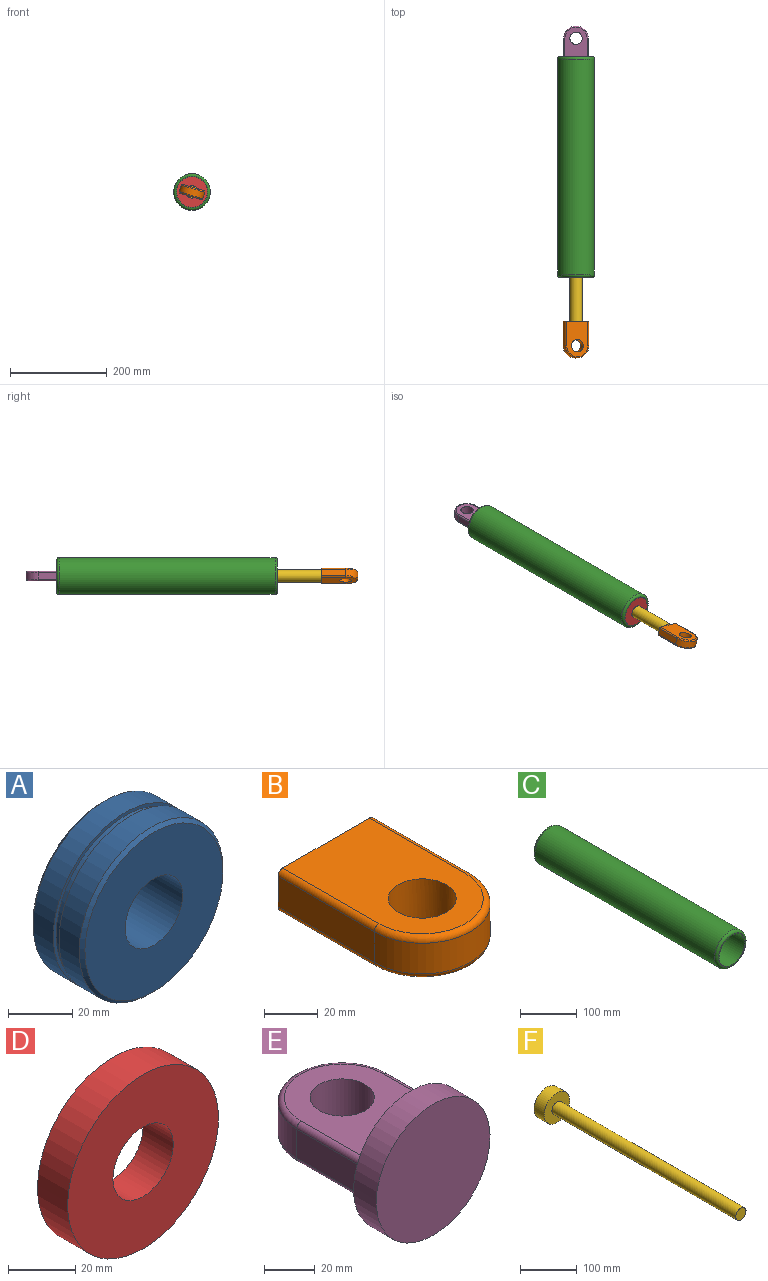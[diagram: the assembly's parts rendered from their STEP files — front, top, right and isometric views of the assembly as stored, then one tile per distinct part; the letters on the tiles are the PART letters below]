
ASSEMBLY  parts=6 mates=5
PART A: 10 faces, bbox 63.5x22.9x63.5 mm
  f0: cylinder r=31.75mm len=63.5mm, axis (0,1,0), area 1773.5mm2, adj f1,f8
  f1: plane 63.5x63.5mm, normal (0,-1,0), area 248.3mm2, adj f0,f3
  f2: plane 60.96x60.96mm, normal (0,1,0), area 2411.9mm2, adj f7,f8
  f3: cylinder r=30.48mm len=60.96mm, axis (0,1,0), area 486.4mm2, adj f1,f6
  f4: cylinder r=31.75mm len=63.5mm, axis (0,1,0), area 1773.5mm2, adj f6,f9
  f5: plane 60.96x60.96mm, normal (0,-1,0), area 2411.9mm2, adj f7,f9
  f6: plane 63.5x63.5mm, normal (0,1,0), area 248.3mm2, adj f3,f4
  f7: cylinder r=12.7mm len=25.4mm, axis (0,-1,0), area 1824.1mm2, adj f2,f5
  f8: cone r=31.75mm half-angle=45deg, axis (0,-1,0), area 351.1mm2, adj f0,f2
  f9: cone r=30.48mm half-angle=45deg, axis (0,1,0), area 351.1mm2, adj f4,f5
PART B: 13 faces, bbox 55x78.3x19.1 mm
  f0: plane 73.66x45.72mm, normal (0,0,1), area 2636.7mm2, adj f4,f6,f7,f8,f9
  f1: plane 50.8x13.97mm, normal (-1,0,0), area 709.7mm2, adj f4,f5,f7,f11
  f2: plane 73.66x45.72mm, normal (0,0,-1), area 2636.7mm2, adj f4,f6,f10,f11,f12
  f3: plane 50.8x13.97mm, normal (1,0,0), area 709.7mm2, adj f4,f5,f8,f10
  f4: plane 50.8x19.05mm, normal (0,1,0), area 962.2mm2, adj f0,f1,f2,f3,f7,f8,f10,f11
  f5: cylinder r=25.4mm len=50.8mm, axis (0,0,-1), area 1114.8mm2, adj f1,f3,f9,f12
  f6: cylinder r=12.7mm len=25.4mm, axis (0,0,-1), area 1520.1mm2, adj f0,f2
  f7: cylinder r=2.54mm len=50.8mm, axis (0,-1,0), area 202.7mm2, adj f0,f1,f4,f9
  f8: cylinder r=2.54mm len=50.8mm, axis (0,1,0), area 202.7mm2, adj f0,f3,f4,f9
  f9: torus R=22.86mm, axis (0,0,1), area 306.8mm2, adj f0,f5,f7,f8
  f10: cylinder r=2.54mm len=50.8mm, axis (0,-1,0), area 202.7mm2, adj f2,f3,f4,f12
  f11: cylinder r=2.54mm len=50.8mm, axis (0,1,0), area 202.7mm2, adj f1,f2,f4,f12
  f12: torus R=22.86mm, axis (0,0,1), area 306.8mm2, adj f2,f5,f10,f11
PART C: 6 faces, bbox 82.5x457.2x82.5 mm
  f0: cylinder r=31.75mm len=457.2mm, axis (0,1,0), area 91207.3mm2, adj f2,f3
  f1: cylinder r=38.1mm len=447.04mm, axis (0,1,0), area 107016.6mm2, adj f4,f5
  f2: plane 66.04x66.04mm, normal (0,-1,0), area 258.4mm2, adj f0,f5
  f3: plane 66.04x66.04mm, normal (0,1,0), area 258.4mm2, adj f0,f4
  f4: torus R=33.02mm, axis (0,-1,0), area 1817.7mm2, adj f1,f3
  f5: torus R=33.02mm, axis (0,-1,0), area 1817.7mm2, adj f1,f2
PART D: 4 faces, bbox 63.5x12.7x63.5 mm
  f0: cylinder r=12.7mm len=25.4mm, axis (0,1,0), area 1013.4mm2, adj f2,f3
  f1: cylinder r=31.75mm len=63.5mm, axis (0,1,0), area 2533.5mm2, adj f2,f3
  f2: plane 63.5x63.5mm, normal (0,-1,0), area 2660.2mm2, adj f0,f1
  f3: plane 63.5x63.5mm, normal (0,1,0), area 2660.2mm2, adj f0,f1
PART E: 15 faces, bbox 63.5x78.3x63.5 mm
  f0: cylinder r=31.75mm len=63.5mm, axis (0,1,0), area 2533.5mm2, adj f5,f14
  f1: plane 60.96x45.72mm, normal (0,0,1), area 2056.1mm2, adj f5,f7,f8,f9,f13
  f2: plane 38.1x13.97mm, normal (-1,0,0), area 532.3mm2, adj f5,f6,f7,f11
  f3: plane 60.96x45.72mm, normal (0,0,-1), area 2056.1mm2, adj f5,f10,f11,f12,f13
  f4: plane 38.1x13.97mm, normal (1,0,0), area 532.3mm2, adj f5,f6,f8,f10
  f5: plane 63.5x63.5mm, normal (0,1,0), area 2204.7mm2, adj f0,f1,f2,f3,f4,f7,f8,f10
  f6: cylinder r=25.4mm len=50.8mm, axis (0,0,-1), area 1114.8mm2, adj f2,f4,f9,f12
  f7: cylinder r=2.54mm len=38.1mm, axis (0,1,0), area 152mm2, adj f1,f2,f5,f9
  f8: cylinder r=2.54mm len=38.1mm, axis (0,-1,0), area 152mm2, adj f1,f4,f5,f9
  f9: torus R=22.86mm, axis (0,0,1), area 306.8mm2, adj f1,f6,f7,f8
  f10: cylinder r=2.54mm len=38.1mm, axis (0,1,0), area 152mm2, adj f3,f4,f5,f12
  f11: cylinder r=2.54mm len=38.1mm, axis (0,-1,0), area 152mm2, adj f2,f3,f5,f12
  f12: torus R=22.86mm, axis (0,0,1), area 306.8mm2, adj f3,f6,f10,f11
  f13: cylinder r=12.7mm len=25.4mm, axis (0,0,1), area 1520.1mm2, adj f1,f3
  f14: plane 63.5x63.5mm, normal (0,-1,0), area 3166.9mm2, adj f0
PART F: 5 faces, bbox 63.5x482.6x63.5 mm
  f0: cylinder r=31.75mm len=63.5mm, axis (0,1,0), area 5067.1mm2, adj f1,f2
  f1: plane 63.5x63.5mm, normal (0,-1,0), area 2660.2mm2, adj f0,f3
  f2: plane 63.5x63.5mm, normal (0,1,0), area 3166.9mm2, adj f0
  f3: cylinder r=12.7mm len=457.2mm, axis (0,1,0), area 36482.9mm2, adj f1,f4
  f4: plane 25.4x25.4mm, normal (0,-1,0), area 506.7mm2, adj f3
PLACE A t=(0.51,35.22,-0.95)mm
PLACE B rot(axis=(0,1,0),16.4deg) t=(0.51,-319.47,-0.95)mm
PLACE C t=(0.51,-0.34,-0.95)mm fixed
PLACE D t=(0.51,-222.59,-0.95)mm
PLACE E rot(axis=(0,1,0),180deg) t=(0.51,215.56,-0.95)mm
PLACE F rot(axis=(0,1,0),16.4deg) t=(0.51,150.43,-0.95)mm
MATE cylindrical F.f0 <-> D.f0  axis (0,-1,0) through (0.51,137.73,-0.95)mm
MATE fastened F.f3 <-> B.f4  axis (0,1,0) through (0.51,-319.47,-0.95)mm
MATE slider A.f7 <-> D.f0  axis (0,-1,0) through (0.51,12.36,-0.95)mm
MATE fastened E.f0 <-> C.f0  axis (0,1,0) through (0.51,228.26,-0.95)mm
MATE fastened D.f1 <-> C.f0  axis (0,-1,0) through (0.51,-228.94,-0.95)mm
